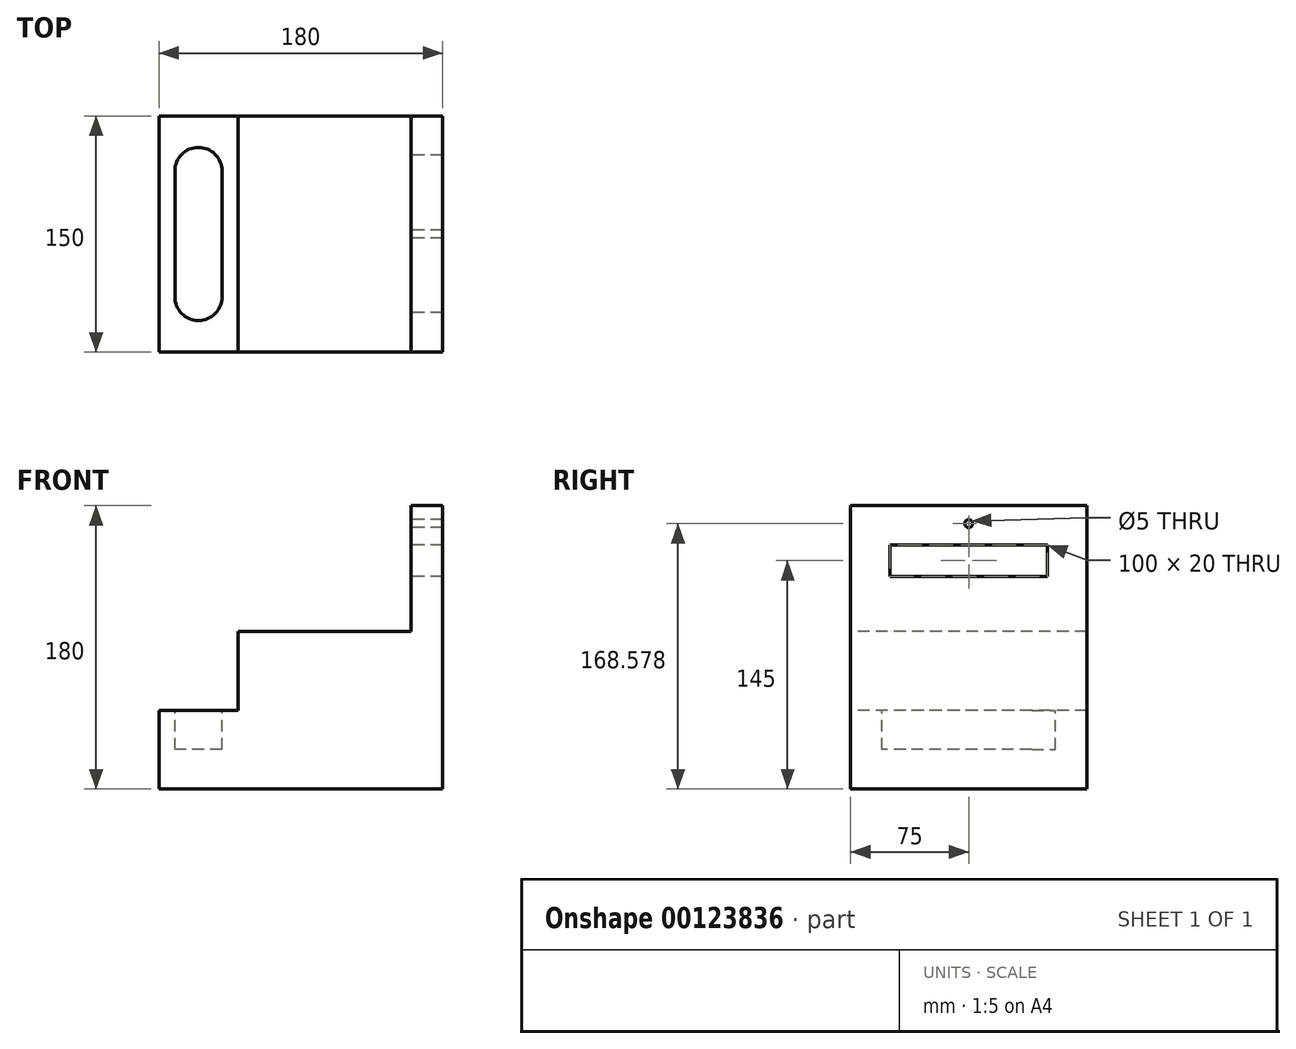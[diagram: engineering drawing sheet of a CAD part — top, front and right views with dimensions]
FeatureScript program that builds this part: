
annotation { "Feature Type Name" : "Feature", "Feature Type Description" : "" }
export const myFeature = defineFeature(function(context is Context, id is Id, definition is map)
    precondition{}
    {
        {
            var Q0;
            Q0=qCreatedBy(makeId("Front.planeOp"),FACE);
            var sketch = newSketch(context, id + "F0", { "sketchPlane" : qUnion([Q0])});
            skLineSegment(sketch, "E0.bottom", {"start": v(90, 90) * mm, "end": v(70, 90) * mm});
            skLineSegment(sketch, "E0.top", {"start": v(90, -90) * mm, "end": v(-90, -90) * mm});
            skLineSegment(sketch, "E0.left", {"start": v(90, 90) * mm, "end": v(90, -90) * mm});
            skLineSegment(sketch, "E0.right", {"start": v(-90, -40) * mm, "end": v(-90, -90) * mm});
            skPoint(sketch, "E0.middle", {"position": v(0, 0) * mm});
            skLineSegment(sketch, "E1", {"start": v(-90, -90) * mm, "end": v(-90, -40) * mm});
            skLineSegment(sketch, "E2", {"start": v(-90, -40) * mm, "end": v(-40, -40) * mm});
            skLineSegment(sketch, "E3", {"start": v(-40, -40) * mm, "end": v(-40, 10) * mm});
            skLineSegment(sketch, "E4", {"start": v(-40, 10) * mm, "end": v(70, 10) * mm});
            skLineSegment(sketch, "E5", {"start": v(70, 10) * mm, "end": v(70, 90) * mm});
            skLineSegment(sketch, "E6", {"start": v(70, 90) * mm, "end": v(90, 90) * mm});
            skPoint(sketch, "E7.orphan", {"position": v(-90, 90) * mm});
            skSolve(sketch);
        }
        {
            var Q0;
            Q0 = qSketchRegion(id + "F0", true);
            var Q1;
            Q1=makeQuery(id+"F0.imprint","IMPRINT",FACE,{"disambiguationData":[TD([[makeQuery(id+"F0.imprint","IMPRINT",EDGE,{"derivedFrom":sQuery(id+"F0.wireOp",EDGE,"E0.top")}),-1.0]])]});
            extrude(context, id + "F1", {"entities" : qUnion([Q0, Q1]), "oppositeDirection" : true, "depth" : 150 * mm});
        }
        {
            var Q0;
            Q0=makeQuery(id+"F1.opExtrude","SWEPT_FACE",FACE,{"disambiguationData":[OSD([sQuery(id+"F0.wireOp",EDGE,"E5")])]});
            var sketch = newSketch(context, id + "F2", { "sketchPlane" : qUnion([Q0])});
            skCircle(sketch, "E8", {"center": v(-75, 78.58) * mm, "radius": 2.5 * mm});
            skSolve(sketch);
        }
        {
            var Q0;
            Q0 = qSketchRegion(id + "F2", true);
            extrude(context, id + "F3", {"entities" : qUnion([Q0]), "operationType" : NewBodyOperationType.REMOVE, "endBound" : BoundingType.THROUGH_ALL, "oppositeDirection" : true, "depth" : 25.4 * mm});
        }
        {
            var Q0;
            Q0=makeQuery(id+"F1.opExtrude","SWEPT_FACE",FACE,{"disambiguationData":[OSD([sQuery(id+"F0.wireOp",EDGE,"E5")])]});
            var sketch = newSketch(context, id + "F4", { "sketchPlane" : qUnion([Q0])});
            skLineSegment(sketch, "E9.bottom", {"start": v(-25, 65) * mm, "end": v(-125, 65) * mm});
            skLineSegment(sketch, "E9.top", {"start": v(-25, 45) * mm, "end": v(-125, 45) * mm});
            skLineSegment(sketch, "E9.left", {"start": v(-25, 65) * mm, "end": v(-25, 45) * mm});
            skLineSegment(sketch, "E9.right", {"start": v(-125, 65) * mm, "end": v(-125, 45) * mm});
            skSolve(sketch);
        }
        {
            var Q0;
            Q0 = qSketchRegion(id + "F4", true);
            extrude(context, id + "F5", {"entities" : qUnion([Q0]), "operationType" : NewBodyOperationType.REMOVE, "endBound" : BoundingType.THROUGH_ALL, "oppositeDirection" : true, "depth" : 25.4 * mm});
        }
        {
            var Q0;
            Q0=makeQuery(id+"F1.opExtrude","SWEPT_FACE",FACE,{"disambiguationData":[OSD([sQuery(id+"F0.wireOp",EDGE,"E2")])]});
            var sketch = newSketch(context, id + "F6", { "sketchPlane" : qUnion([Q0])});
            skLineSegment(sketch, "E10.left", {"start": v(-50, 115) * mm, "end": v(-50, 35) * mm});
            skLineSegment(sketch, "E10.right", {"start": v(-80, 115) * mm, "end": v(-80, 35) * mm});
            skArc(sketch, "E11", {"start": v(-50, 115) * mm, "mid": v(-65, 130) * mm, "end": v(-80, 115) * mm});
            skArc(sketch, "E12", {"start": v(-80, 35) * mm, "mid": v(-65, 20) * mm, "end": v(-50, 35) * mm});
            skSolve(sketch);
        }
        {
            var Q0;
            Q0 = qSketchRegion(id + "F6", true);
            extrude(context, id + "F7", {"entities" : qUnion([Q0]), "operationType" : NewBodyOperationType.REMOVE, "oppositeDirection" : true, "depth" : 25 * mm});
        }
    });
